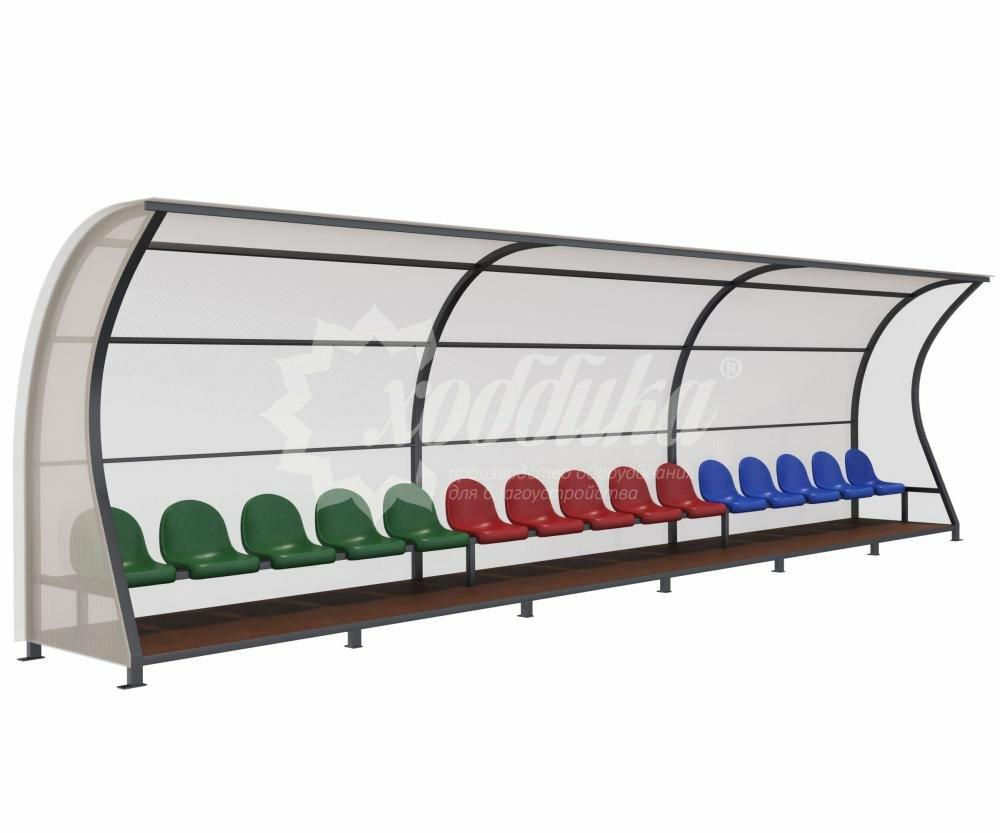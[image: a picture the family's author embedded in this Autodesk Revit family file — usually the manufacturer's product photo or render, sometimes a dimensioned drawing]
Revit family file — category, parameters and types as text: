
# Revit family: 30245 Скамейка для запасных игроков на 15 мест с навесом «Спектра-15» Хоббика
name_source: partatom
category: Антураж
revit_build: Autodesk Revit 2018 (Build: 20180423_1000(x64)
units: mm (PartAtom-declared; Revit-internal decimal feet)

## family parameters
Всегда вертикально = Да
Источник визуального образа = Геометрия семейства
На основе рабочей плоскости = Нет
Общий = Нет
При загрузке вырезать с полостями = Нет
Точка расчета площади = Нет

## types (1)
- Скамейка для запасных игроков на 15 мест с навесом «Спектра-15»
    URL = https://hobbyka.ru
    Артикул товара = Арт. 30245
    Высота = 2135 мм
    Группа модели = Мобильные и стационарные трибуны
    Длина = 7800 мм
    Изготовитель = ООО «Хоббика»
    Изображение типоразмера = Скамейка для запасных игроков на 15 мест с навесом «Спектра-15» Арт 30245.jpg
    Материал изделия = Сталь, поликарбонат, пластик
    Описание = Скамейка для запасных игроков на 15 мест с навесом «Спектра-15»
    Цвет каркаса = Сталь
    Цвет навеса = Поликарбонат
    Цвет настила = Настил
    Цвет сидения = Красный
    Ширина = 1450 мм

## geometry (parser evidence)
native form markers: Blend x413, Sweep x3
no freeform markers — native parametric forms only
